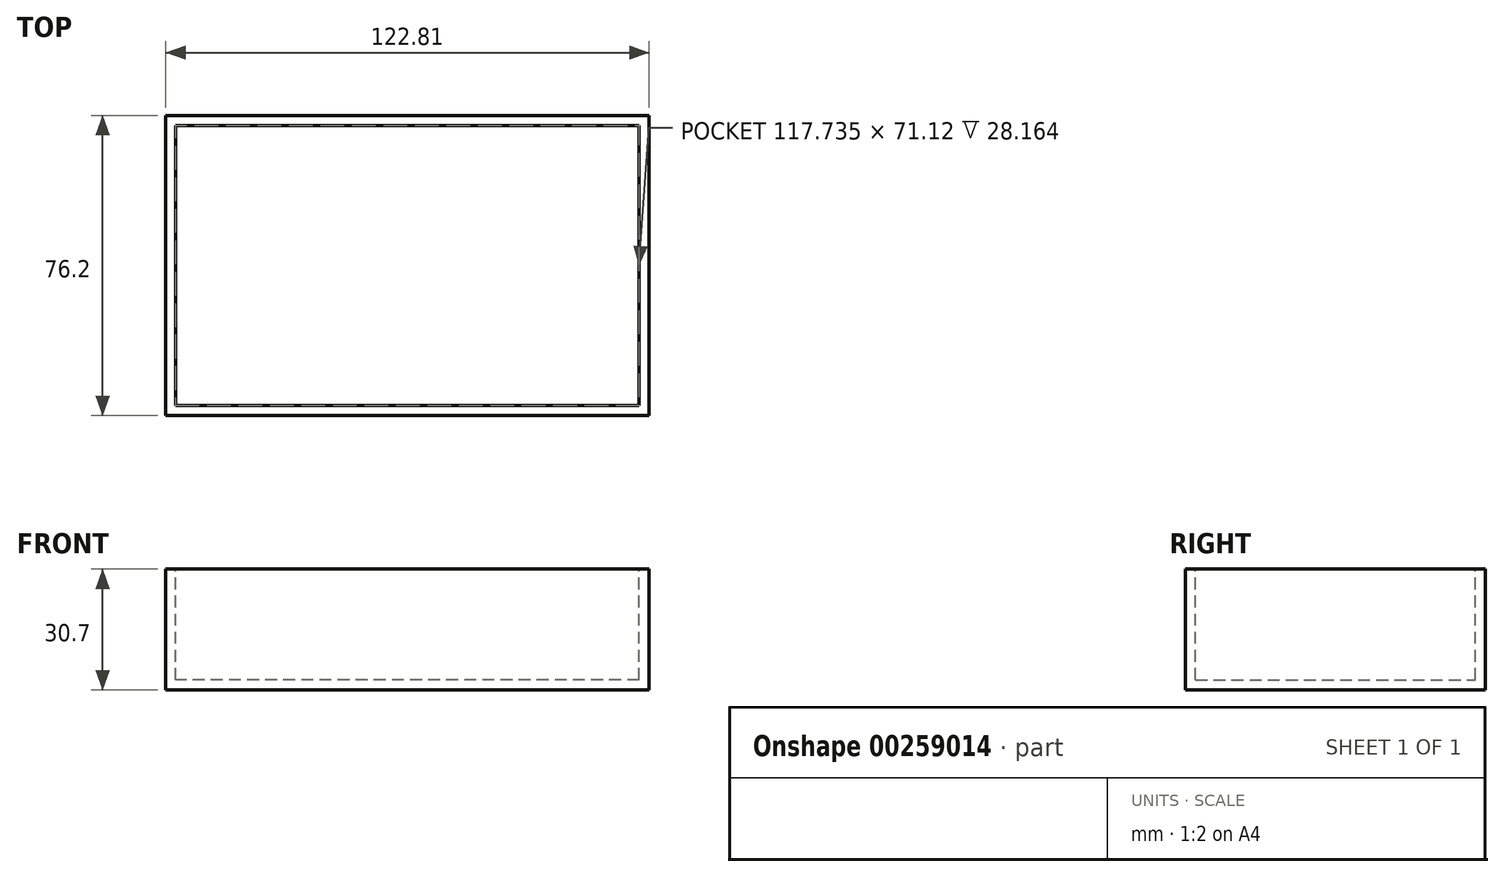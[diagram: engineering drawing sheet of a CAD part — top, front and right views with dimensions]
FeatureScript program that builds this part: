
annotation { "Feature Type Name" : "Feature", "Feature Type Description" : "" }
export const myFeature = defineFeature(function(context is Context, id is Id, definition is map)
    precondition{}
    {
        {
            var Q0;
            Q0=qCreatedBy(makeId("Front.planeOp"),FACE);
            var sketch = newSketch(context, id + "F0", { "sketchPlane" : qUnion([Q0])});
            skLineSegment(sketch, "E0.bottom", {"start": v(29.04, 22.82) * mm, "end": v(-93.77, 22.82) * mm});
            skLineSegment(sketch, "E0.top", {"start": v(29.04, 53.52) * mm, "end": v(-93.77, 53.52) * mm});
            skLineSegment(sketch, "E0.left", {"start": v(29.04, 22.82) * mm, "end": v(29.04, 53.52) * mm});
            skLineSegment(sketch, "E0.right", {"start": v(-93.77, 22.82) * mm, "end": v(-93.77, 53.52) * mm});
            skPoint(sketch, "E0.middle", {"position": v(-32.36, 38.17) * mm});
            skSolve(sketch);
        }
        {
            var Q0;
            Q0 = qSketchRegion(id + "F0", true);
            var Q1;
            Q1=makeQuery(id+"F0.imprint","IMPRINT",FACE,{"disambiguationData":[TD([[makeQuery(id+"F0.imprint","IMPRINT",EDGE,{"derivedFrom":sQuery(id+"F0.wireOp",EDGE,"E0.bottom")}),-1.0]])]});
            extrude(context, id + "F1", {"entities" : qUnion([Q0, Q1]), "depth" : 76.2 * mm});
        }
        {
            var Q0;
            Q0=makeQuery(id+"F1.opExtrude","SWEPT_FACE",FACE,{"disambiguationData":[OSD([sQuery(id+"F0.wireOp",EDGE,"E0.top")])]});
            shell(context, id + "F2", {"entities" : qUnion([Q0]), "thickness" : 2.54 * mm});
        }
    });
